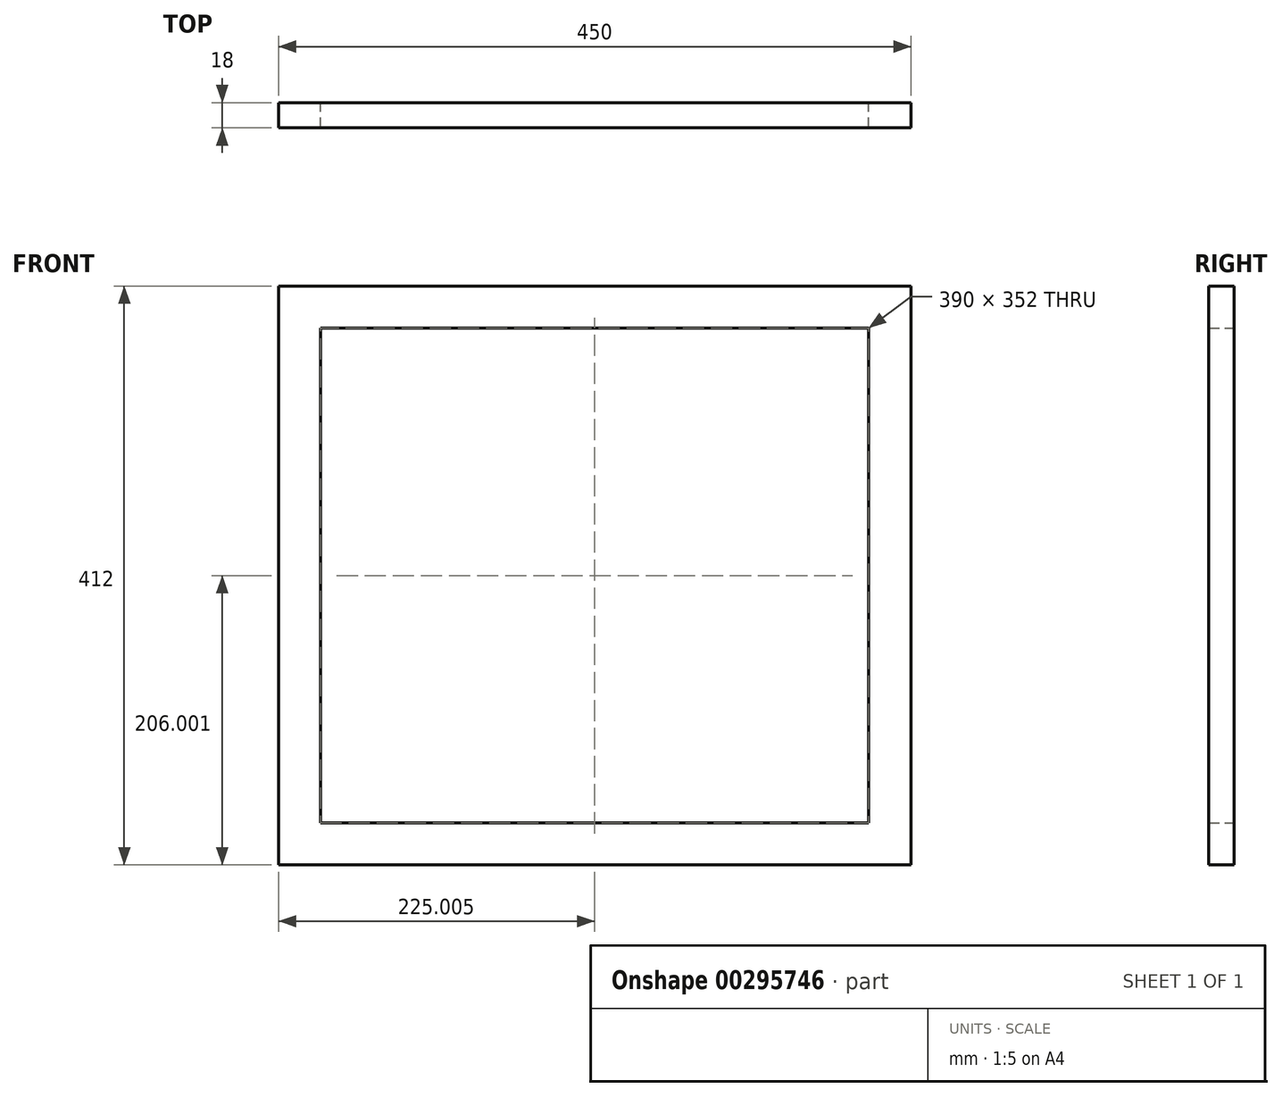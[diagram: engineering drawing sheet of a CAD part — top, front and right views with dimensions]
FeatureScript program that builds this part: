
annotation { "Feature Type Name" : "Feature", "Feature Type Description" : "" }
export const myFeature = defineFeature(function(context is Context, id is Id, definition is map)
    precondition{}
    {
        {
            var Q0;
            Q0=qCreatedBy(makeId("Front.planeOp"),FACE);
            var sketch = newSketch(context, id + "F0", { "sketchPlane" : qUnion([Q0])});
            skLineSegment(sketch, "E0.bottom", {"start": v(-251.9, 219.92) * mm, "end": v(198.1, 219.92) * mm});
            skLineSegment(sketch, "E0.top", {"start": v(-251.9, -192.08) * mm, "end": v(198.1, -192.08) * mm});
            skLineSegment(sketch, "E0.left", {"start": v(-251.9, 219.92) * mm, "end": v(-251.9, -192.08) * mm});
            skLineSegment(sketch, "E0.right", {"start": v(198.1, 219.92) * mm, "end": v(198.1, -192.08) * mm});
            skLineSegment(sketch, "E1.bottom", {"start": v(-221.9, 189.92) * mm, "end": v(168.1, 189.92) * mm});
            skLineSegment(sketch, "E1.top", {"start": v(-221.9, -162.08) * mm, "end": v(168.1, -162.08) * mm});
            skLineSegment(sketch, "E1.left", {"start": v(-221.9, 189.92) * mm, "end": v(-221.9, -162.08) * mm});
            skLineSegment(sketch, "E1.right", {"start": v(168.1, 189.92) * mm, "end": v(168.1, -162.08) * mm});
            skSolve(sketch);
        }
        {
            var Q0;
            Q0 = qSketchRegion(id + "F0", true);
            extrude(context, id + "F1", {"entities" : qUnion([Q0]), "depth" : 18 * mm});
        }
    });
